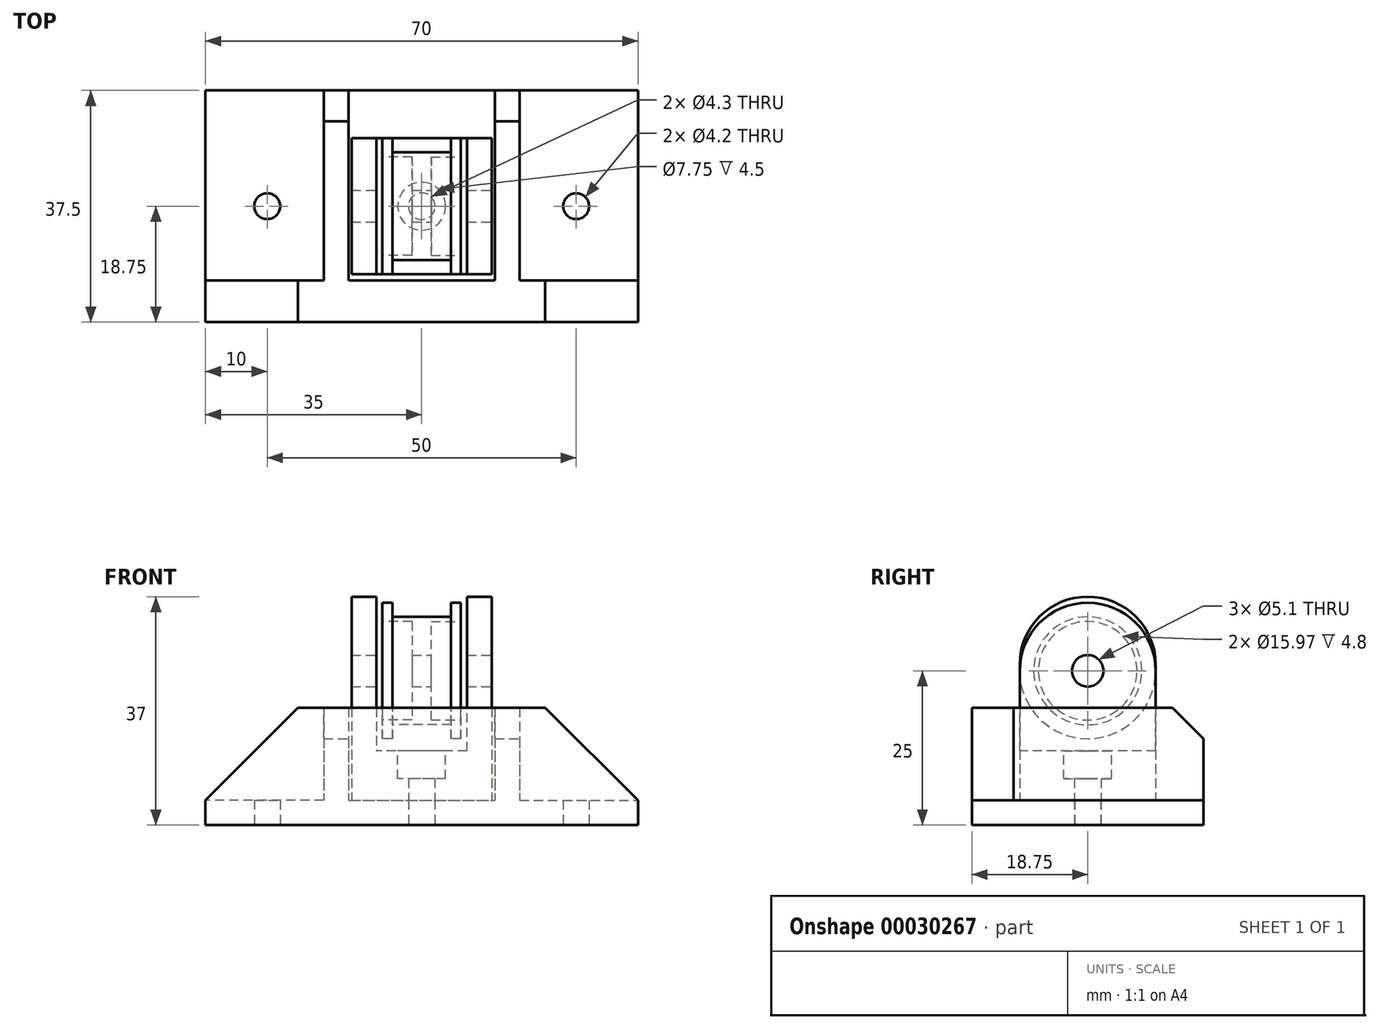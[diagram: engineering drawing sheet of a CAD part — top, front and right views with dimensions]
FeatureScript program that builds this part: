
annotation { "Feature Type Name" : "Feature", "Feature Type Description" : "" }
export const myFeature = defineFeature(function(context is Context, id is Id, definition is map)
    precondition{}
    {
        {
            var Q0;
            Q0=qCreatedBy(makeId("Front.planeOp"),FACE);
            var sketch = newSketch(context, id + "F0", { "sketchPlane" : qUnion([Q0])});
            skLineSegment(sketch, "E0", {"start": v(-16.28, 0) * mm, "end": v(18.84, 0) * mm, "construction": true});
            skLineSegment(sketch, "E1", {"start": v(-6.35, 0) * mm, "end": v(-6.35, 11) * mm});
            skLineSegment(sketch, "E2", {"start": v(-6.35, 11) * mm, "end": v(-4.75, 11) * mm});
            skLineSegment(sketch, "E3", {"start": v(-4.75, 11) * mm, "end": v(-4.75, 8.75) * mm});
            skLineSegment(sketch, "E4", {"start": v(-4.75, 8.75) * mm, "end": v(0, 8.75) * mm});
            skLineSegment(sketch, "E5", {"start": v(0, 18.26) * mm, "end": v(0, -4.95) * mm, "construction": true});
            skLineSegment(sketch, "E6.MirrorCS", {"start": v(6.35, 0) * mm, "end": v(6.35, 11) * mm});
            skLineSegment(sketch, "E7.MirrorCS", {"start": v(6.35, 11) * mm, "end": v(4.75, 11) * mm});
            skLineSegment(sketch, "E8.MirrorCS", {"start": v(4.75, 8.75) * mm, "end": v(0, 8.75) * mm});
            skLineSegment(sketch, "E9.MirrorCS", {"start": v(4.75, 11) * mm, "end": v(4.75, 8.75) * mm});
            skLineSegment(sketch, "E10", {"start": v(-6.35, 0) * mm, "end": v(6.35, 0) * mm});
            skSolve(sketch);
        }
        {
            var Q0;
            Q0 = qSketchRegion(id + "F0", true);
            var Q1;
            Q1=sQuery(id+"F0.wireOp",EDGE,"E1");
            var Q2;
            Q2=sQuery(id+"F0.wireOp",EDGE,"E2");
            var Q3;
            Q3=sQuery(id+"F0.wireOp",EDGE,"E3");
            var Q4;
            Q4=sQuery(id+"F0.wireOp",EDGE,"E4");
            var Q5;
            Q5=sQuery(id+"F0.wireOp",EDGE,"E8.MirrorCS");
            var Q6;
            Q6=sQuery(id+"F0.wireOp",EDGE,"E9.MirrorCS");
            var Q7;
            Q7=sQuery(id+"F0.wireOp",EDGE,"E7.MirrorCS");
            var Q8;
            Q8=sQuery(id+"F0.wireOp",EDGE,"E6.MirrorCS");
            var Q9;
            Q9=sQuery(id+"F0.wireOp",EDGE,"E0");
            revolve(context, id + "F1", {"entities" : qUnion([Q0]), "surfaceEntities" : qUnion([Q1, Q2, Q3, Q4, Q5, Q6, Q7, Q8]), "axis" : qUnion([Q9]), "revolveType" : RevolveType.FULL});
        }
        {
            var Q0;
            Q0=makeQuery(id+"F1.opRevolve","SWEPT_FACE",FACE,{"disambiguationData":[OSD([sQuery(id+"F0.wireOp",EDGE,"E1")])]});
            var sketch = newSketch(context, id + "F2", { "sketchPlane" : qUnion([Q0])});
            skCircle(sketch, "E11", {"center": v(0, 0) * mm, "radius": 2.5 * mm});
            skSolve(sketch);
        }
        {
            var Q0;
            Q0=makeQuery(id+"F1.opRevolve","SWEPT_FACE",FACE,{"disambiguationData":[OSD([sQuery(id+"F0.wireOp",EDGE,"E1")])]});
            var sketch = newSketch(context, id + "F3", { "sketchPlane" : qUnion([Q0])});
            skCircle(sketch, "E12", {"center": v(0, 0) * mm, "radius": 7.99 * mm});
            skSolve(sketch);
        }
        {
            var Q0;
            Q0 = qSketchRegion(id + "F3", true);
            extrude(context, id + "F4", {"entities" : qUnion([Q0]), "operationType" : NewBodyOperationType.REMOVE, "oppositeDirection" : true, "depth" : 4.8 * mm});
        }
        {
            var Q0;
            Q0=makeQuery(id+"F1.opRevolve","SWEPT_FACE",FACE,{"disambiguationData":[OSD([sQuery(id+"F0.wireOp",EDGE,"E6.MirrorCS")])]});
            var sketch = newSketch(context, id + "F5", { "sketchPlane" : qUnion([Q0])});
            skCircle(sketch, "E13", {"center": v(0, 0) * mm, "radius": 7.99 * mm});
            skSolve(sketch);
        }
        {
            var Q0;
            Q0 = qSketchRegion(id + "F5", true);
            extrude(context, id + "F6", {"entities" : qUnion([Q0]), "operationType" : NewBodyOperationType.REMOVE, "oppositeDirection" : true, "depth" : 4.8 * mm});
        }
        {
            var Q0;
            Q0 = qSketchRegion(id + "F2", true);
            extrude(context, id + "F7", {"entities" : qUnion([Q0]), "operationType" : NewBodyOperationType.REMOVE, "endBound" : BoundingType.THROUGH_ALL, "oppositeDirection" : true, "depth" : 25 * mm});
        }
        {
            var Q0;
            Q0=qCreatedBy(makeId("Front.planeOp"),FACE);
            cPlane(context, id + "F8", {"entities" : qUnion([Q0]), "cplaneType" : CPlaneType.OFFSET, "offset" : 11 * mm, "width" : 150 * mm, "height" : 150 * mm});
        }
        {
            var Q0;
            Q0=qCreatedBy(id+"F8.planeOp",FACE);
            var sketch = newSketch(context, id + "F9", { "sketchPlane" : qUnion([Q0])});
            skLineSegment(sketch, "E14", {"start": v(0, 64.01) * mm, "end": v(0, -67.15) * mm, "construction": true});
            skLineSegment(sketch, "E15", {"start": v(7.35, 0) * mm, "end": v(7.35, 12) * mm});
            skLineSegment(sketch, "E16", {"start": v(7.35, 12) * mm, "end": v(11.35, 12) * mm});
            skLineSegment(sketch, "E17", {"start": v(7.35, 0) * mm, "end": v(7.35, -13) * mm});
            skLineSegment(sketch, "E18", {"start": v(7.35, -13) * mm, "end": v(0, -13) * mm});
            skLineSegment(sketch, "E19", {"start": v(11.35, 12) * mm, "end": v(11.35, -21) * mm});
            skLineSegment(sketch, "E20", {"start": v(11.35, -21) * mm, "end": v(0, -21) * mm});
            skLineSegment(sketch, "E21.MirrorCS", {"start": v(-7.35, 0) * mm, "end": v(-7.35, -13) * mm});
            skLineSegment(sketch, "E22.MirrorCS", {"start": v(-7.35, -13) * mm, "end": v(0, -13) * mm});
            skLineSegment(sketch, "E23.MirrorCS", {"start": v(-11.35, -21) * mm, "end": v(0, -21) * mm});
            skLineSegment(sketch, "E24.MirrorCS", {"start": v(-11.35, 12) * mm, "end": v(-11.35, -21) * mm});
            skLineSegment(sketch, "E25.MirrorCS", {"start": v(-7.35, 0) * mm, "end": v(-7.35, 12) * mm});
            skLineSegment(sketch, "E26.MirrorCS", {"start": v(-7.35, 12) * mm, "end": v(-11.35, 12) * mm});
            skSolve(sketch);
        }
        {
            var Q0;
            Q0 = qSketchRegion(id + "F9", true);
            extrude(context, id + "F10", {"entities" : qUnion([Q0]), "oppositeDirection" : true, "depth" : 22 * mm});
        }
        {
            var Q0;
            Q0=makeQuery(id+"F10.opExtrude","SWEPT_FACE",FACE,{"disambiguationData":[OSD([sQuery(id+"F9.wireOp",EDGE,"E19")])]});
            var sketch = newSketch(context, id + "F11", { "sketchPlane" : qUnion([Q0])});
            skCircle(sketch, "E27", {"center": v(0, 0) * mm, "radius": 2.55 * mm});
            skSolve(sketch);
        }
        {
            var Q0;
            Q0 = qSketchRegion(id + "F11", true);
            extrude(context, id + "F12", {"entities" : qUnion([Q0]), "operationType" : NewBodyOperationType.REMOVE, "endBound" : BoundingType.THROUGH_ALL, "oppositeDirection" : true, "depth" : 25 * mm});
        }
        {
            var Q0;
            Q0=makeQuery(id+"F10.opExtrude","CAP_EDGE",EDGE,{"disambiguationData":[OSD([sQuery(id+"F9.wireOp",EDGE,"E26.MirrorCS")])],"isStart":false});
            var Q1;
            Q1=makeQuery(id+"F10.opExtrude","CAP_EDGE",EDGE,{"disambiguationData":[OSD([sQuery(id+"F9.wireOp",EDGE,"E16")])],"isStart":false});
            var Q2;
            Q2=makeQuery(id+"F10.opExtrude","CAP_EDGE",EDGE,{"disambiguationData":[OSD([sQuery(id+"F9.wireOp",EDGE,"E26.MirrorCS")])],"isStart":true});
            var Q3;
            Q3=makeQuery(id+"F10.opExtrude","CAP_EDGE",EDGE,{"disambiguationData":[OSD([sQuery(id+"F9.wireOp",EDGE,"E16")])],"isStart":true});
            fillet(context, id + "F13", {"entities" : qUnion([Q0, Q1, Q2, Q3]), "radius" : 11 * mm, "tangentPropagation" : true, "allowEdgeOverflow" : false});
        }
        {
            var Q0;
            Q0=makeQuery(id+"F10.opExtrude","SWEPT_FACE",FACE,{"disambiguationData":[OSD([sQuery(id+"F9.wireOp",EDGE,"E20"),sQuery(id+"F9.wireOp",EDGE,"E23.MirrorCS")])]});
            var sketch = newSketch(context, id + "F14", { "sketchPlane" : qUnion([Q0])});
            skCircle(sketch, "E28", {"center": v(0, 0) * mm, "radius": 2.15 * mm});
            skSolve(sketch);
        }
        {
            var Q0;
            Q0 = qSketchRegion(id + "F14", true);
            extrude(context, id + "F15", {"entities" : qUnion([Q0]), "operationType" : NewBodyOperationType.REMOVE, "endBound" : BoundingType.UP_TO_NEXT, "oppositeDirection" : true, "depth" : 25 * mm});
        }
        {
            var Q0;
            Q0=makeQuery(id+"F10.opExtrude","SWEPT_FACE",FACE,{"disambiguationData":[OSD([sQuery(id+"F9.wireOp",EDGE,"E18"),sQuery(id+"F9.wireOp",EDGE,"E22.MirrorCS")])]});
            var sketch = newSketch(context, id + "F16", { "sketchPlane" : qUnion([Q0])});
            skCircle(sketch, "E29", {"center": v(0, 0) * mm, "radius": 3.88 * mm});
            skSolve(sketch);
        }
        {
            var Q0;
            Q0 = qSketchRegion(id + "F16", true);
            extrude(context, id + "F17", {"entities" : qUnion([Q0]), "operationType" : NewBodyOperationType.REMOVE, "oppositeDirection" : true, "depth" : 4.5 * mm});
        }
        {
            var Q0;
            Q0=makeQuery(id+"F10.opExtrude","SWEPT_FACE",FACE,{"disambiguationData":[OSD([sQuery(id+"F9.wireOp",EDGE,"E20"),sQuery(id+"F9.wireOp",EDGE,"E23.MirrorCS")])]});
            var sketch = newSketch(context, id + "F18", { "sketchPlane" : qUnion([Q0])});
            skLineSegment(sketch, "E30.rect.bottom", {"start": v(35, 18.75) * mm, "end": v(-35, 18.75) * mm});
            skLineSegment(sketch, "E30.rect.top", {"start": v(35, -18.75) * mm, "end": v(-35, -18.75) * mm});
            skLineSegment(sketch, "E30.rect.left", {"start": v(35, 18.75) * mm, "end": v(35, -18.75) * mm});
            skLineSegment(sketch, "E30.rect.right", {"start": v(-35, 18.75) * mm, "end": v(-35, -18.75) * mm});
            skPoint(sketch, "E30.rect.middle", {"position": v(0, 0) * mm});
            skSolve(sketch);
        }
        {
            var Q0;
            Q0 = qSketchRegion(id + "F18", true);
            extrude(context, id + "F19", {"entities" : qUnion([Q0]), "depth" : 4 * mm});
        }
        {
            var Q0;
            Q0=makeQuery(id+"F19.opExtrude","CAP_FACE",FACE,{"disambiguationData":[OSD([sQuery(id+"F18.wireOp",EDGE,"E30.rect.bottom"),sQuery(id+"F18.wireOp",EDGE,"E30.rect.top"),sQuery(id+"F18.wireOp",EDGE,"E30.rect.left"),sQuery(id+"F18.wireOp",EDGE,"E30.rect.right")])],"isStart":true});
            var sketch = newSketch(context, id + "F20", { "sketchPlane" : qUnion([Q0])});
            skLineSegment(sketch, "E31.bottom", {"start": v(-11.85, -18.75) * mm, "end": v(-15.85, -18.75) * mm});
            skLineSegment(sketch, "E31.top", {"start": v(-11.85, 18.75) * mm, "end": v(-15.85, 18.75) * mm});
            skLineSegment(sketch, "E31.left", {"start": v(-11.85, -18.75) * mm, "end": v(-11.85, 18.75) * mm});
            skLineSegment(sketch, "E31.right", {"start": v(-15.85, -18.75) * mm, "end": v(-15.85, 18.75) * mm});
            skLineSegment(sketch, "E32", {"start": v(0, 18.75) * mm, "end": v(0, -18.75) * mm, "construction": true});
            skLineSegment(sketch, "E33.MirrorCS", {"start": v(11.85, -18.75) * mm, "end": v(15.85, -18.75) * mm});
            skLineSegment(sketch, "E34.MirrorCS", {"start": v(15.85, -18.75) * mm, "end": v(15.85, 18.75) * mm});
            skLineSegment(sketch, "E35.MirrorCS", {"start": v(11.85, 18.75) * mm, "end": v(15.85, 18.75) * mm});
            skLineSegment(sketch, "E36.MirrorCS", {"start": v(11.85, -18.75) * mm, "end": v(11.85, 18.75) * mm});
            skSolve(sketch);
        }
        {
            var Q0;
            Q0 = qSketchRegion(id + "F20", true);
            extrude(context, id + "F21", {"entities" : qUnion([Q0]), "operationType" : NewBodyOperationType.ADD, "depth" : 15 * mm});
        }
        {
            var Q0;
            {var subQ0=sQuery(id+"F18.wireOp",EDGE,"E30.rect.bottom");var subQ1=sQuery(id+"F18.wireOp",EDGE,"E30.rect.top");Q0=makeQuery(id+"F21.boolean.opBoolean","SPLIT",FACE,{"disambiguationData":[TD([makeQuery(id+"F21.opExtrude","SWEPT_FACE",FACE,{"disambiguationData":[OSD([sQuery(id+"F20.wireOp",EDGE,"E31.left")])]})])],"derivedFrom":makeQuery(id+"F19.opExtrude","CAP_FACE",FACE,{"disambiguationData":[OSD([subQ0,subQ1,sQuery(id+"F18.wireOp",EDGE,"E30.rect.left"),sQuery(id+"F18.wireOp",EDGE,"E30.rect.right")])],"isStart":true})});}
            var sketch = newSketch(context, id + "F22", { "sketchPlane" : qUnion([Q0])});
            skLineSegment(sketch, "E37.bottom", {"start": v(-35, -18.75) * mm, "end": v(35, -18.75) * mm});
            skLineSegment(sketch, "E37.top", {"start": v(-35, -12) * mm, "end": v(35, -12) * mm});
            skLineSegment(sketch, "E37.left", {"start": v(-35, -18.75) * mm, "end": v(-35, -12) * mm});
            skLineSegment(sketch, "E37.right", {"start": v(35, -18.84) * mm, "end": v(35, -12) * mm});
            skSolve(sketch);
        }
        {
            var Q0;
            Q0 = qSketchRegion(id + "F22", true);
            var Q1;
            Q1=makeQuery(id+"F21.opExtrude","CAP_FACE",FACE,{"disambiguationData":[OSD([sQuery(id+"F20.wireOp",EDGE,"E31.bottom"),sQuery(id+"F20.wireOp",EDGE,"E31.top"),sQuery(id+"F20.wireOp",EDGE,"E31.left"),sQuery(id+"F20.wireOp",EDGE,"E31.right")])],"isStart":false});
            extrude(context, id + "F23", {"entities" : qUnion([Q0]), "operationType" : NewBodyOperationType.ADD, "endBound" : BoundingType.UP_TO_SURFACE, "endBoundEntityFace" : qUnion([Q1]), "depth" : 25 * mm});
        }
        {
            var Q0;
            Q0=makeQuery(id+"F23.opExtrude","CAP_EDGE",EDGE,{"disambiguationData":[OSD([sQuery(id+"F22.wireOp",EDGE,"E37.right")])],"isStart":false});
            var Q1;
            Q1=makeQuery(id+"F23.opExtrude","CAP_EDGE",EDGE,{"disambiguationData":[OSD([sQuery(id+"F22.wireOp",EDGE,"E37.left")])],"isStart":false});
            chamfer(context, id + "F24", {"entities" : qUnion([Q0, Q1]), "width" : 15 * mm, "tangentPropagation" : true});
        }
        {
            var Q0;
            Q0=makeQuery(id+"F21.opExtrude","CAP_EDGE",EDGE,{"disambiguationData":[OSD([sQuery(id+"F20.wireOp",EDGE,"E31.top")])],"isStart":false});
            var Q1;
            Q1=makeQuery(id+"F21.opExtrude","CAP_EDGE",EDGE,{"disambiguationData":[OSD([sQuery(id+"F20.wireOp",EDGE,"E35.MirrorCS")])],"isStart":false});
            chamfer(context, id + "F25", {"entities" : qUnion([Q0, Q1]), "width" : 5 * mm, "tangentPropagation" : true});
        }
        {
            var Q0;
            Q0=makeQuery(id+"F19.opExtrude","CAP_FACE",FACE,{"disambiguationData":[OSD([sQuery(id+"F18.wireOp",EDGE,"E30.rect.bottom"),sQuery(id+"F18.wireOp",EDGE,"E30.rect.top"),sQuery(id+"F18.wireOp",EDGE,"E30.rect.left"),sQuery(id+"F18.wireOp",EDGE,"E30.rect.right")])],"isStart":false});
            var sketch = newSketch(context, id + "F26", { "sketchPlane" : qUnion([Q0])});
            skCircle(sketch, "E38.0", {"center": v(0, 0) * mm, "radius": 2.15 * mm, "construction": true});
            skCircle(sketch, "E39", {"center": v(0, 0) * mm, "radius": 2.15 * mm});
            skSolve(sketch);
        }
        {
            var Q0;
            Q0 = qSketchRegion(id + "F26", true);
            extrude(context, id + "F27", {"entities" : qUnion([Q0]), "operationType" : NewBodyOperationType.REMOVE, "endBound" : BoundingType.UP_TO_NEXT, "oppositeDirection" : true, "depth" : 25 * mm});
        }
        {
            var Q0;
            Q0=makeQuery(id+"F19.opExtrude","CAP_FACE",FACE,{"disambiguationData":[OSD([sQuery(id+"F18.wireOp",EDGE,"E30.rect.bottom"),sQuery(id+"F18.wireOp",EDGE,"E30.rect.top"),sQuery(id+"F18.wireOp",EDGE,"E30.rect.left"),sQuery(id+"F18.wireOp",EDGE,"E30.rect.right")])],"isStart":false});
            var sketch = newSketch(context, id + "F28", { "sketchPlane" : qUnion([Q0])});
            skLineSegment(sketch, "E40", {"start": v(-35, 0) * mm, "end": v(35, 0) * mm, "construction": true});
            skCircle(sketch, "E41", {"center": v(-25, 0) * mm, "radius": 2.1 * mm});
            skCircle(sketch, "E42", {"center": v(25, 0) * mm, "radius": 2.1 * mm});
            skSolve(sketch);
        }
        {
            var Q0;
            Q0 = qSketchRegion(id + "F28", true);
            extrude(context, id + "F29", {"entities" : qUnion([Q0]), "operationType" : NewBodyOperationType.REMOVE, "endBound" : BoundingType.UP_TO_NEXT, "oppositeDirection" : true, "depth" : 25 * mm});
        }
    });
